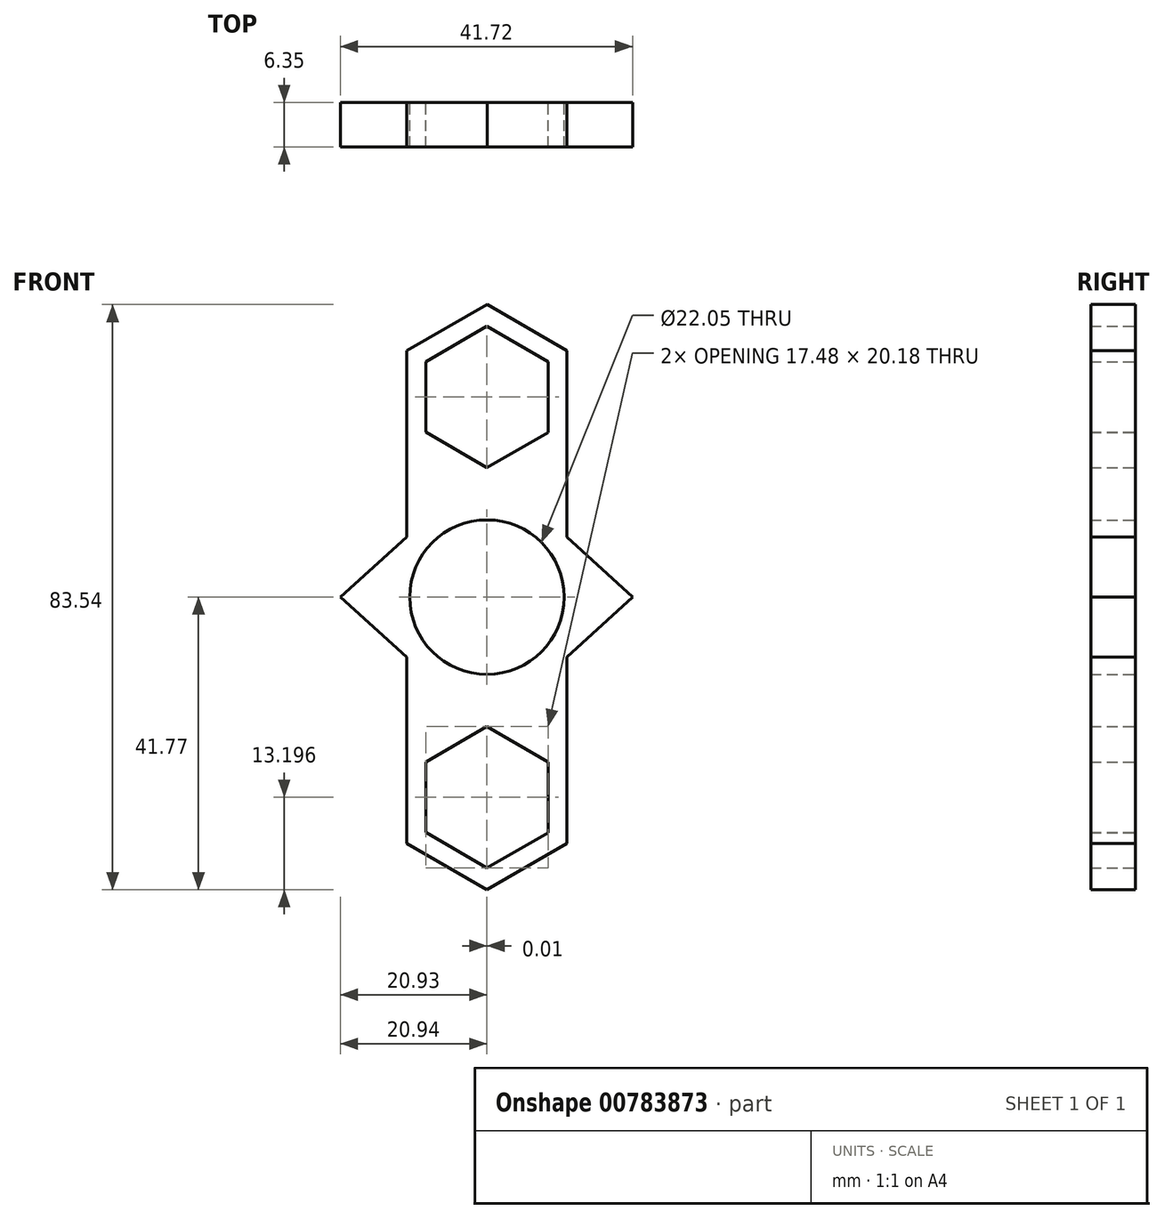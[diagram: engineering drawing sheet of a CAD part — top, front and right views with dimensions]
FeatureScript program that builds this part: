
annotation { "Feature Type Name" : "Feature", "Feature Type Description" : "" }
export const myFeature = defineFeature(function(context is Context, id is Id, definition is map)
    precondition{}
    {
        {
            var Q0;
            Q0=qCreatedBy(makeId("Front.planeOp"),FACE);
            var sketch = newSketch(context, id + "F0", { "sketchPlane" : qUnion([Q0])});
            skCircle(sketch, "E0", {"center": v(0, 0) * mm, "radius": 11.02 * mm});
            skCircle(sketch, "E1", {"center": v(0, 0) * mm, "radius": 14.29 * mm});
            skLineSegment(sketch, "E2", {"start": v(0, 28.58) * mm, "end": v(0, 0) * mm});
            skCircle(sketch, "E3.cCircle", {"center": v(0, 28.58) * mm, "radius": 11.43 * mm, "construction": true});
            skLineSegment(sketch, "E3.0", {"start": v(-0.01, 15.38) * mm, "end": v(-11.44, 21.98) * mm});
            skLineSegment(sketch, "E3.1", {"start": v(-11.44, 21.98) * mm, "end": v(-11.42, 35.18) * mm});
            skLineSegment(sketch, "E3.2", {"start": v(-11.42, 35.18) * mm, "end": v(0.01, 41.77) * mm});
            skLineSegment(sketch, "E3.3", {"start": v(0.01, 41.77) * mm, "end": v(11.44, 35.17) * mm});
            skLineSegment(sketch, "E3.4", {"start": v(11.44, 35.17) * mm, "end": v(11.42, 21.97) * mm});
            skLineSegment(sketch, "E3.5", {"start": v(11.42, 21.97) * mm, "end": v(-0.01, 15.38) * mm});
            skPoint(sketch, "E3.0.midPoint", {"position": v(-5.72, 18.68) * mm});
            skCircle(sketch, "E4.cCircle", {"center": v(0, 28.58) * mm, "radius": 8.74 * mm, "construction": true});
            skLineSegment(sketch, "E4.0", {"start": v(0, 18.49) * mm, "end": v(-8.74, 23.54) * mm});
            skLineSegment(sketch, "E4.1", {"start": v(-8.74, 23.54) * mm, "end": v(-8.73, 33.62) * mm});
            skLineSegment(sketch, "E4.2", {"start": v(-8.73, 33.62) * mm, "end": v(0, 38.66) * mm});
            skLineSegment(sketch, "E4.3", {"start": v(0, 38.66) * mm, "end": v(8.74, 33.61) * mm});
            skLineSegment(sketch, "E4.4", {"start": v(8.74, 33.61) * mm, "end": v(8.73, 23.53) * mm});
            skLineSegment(sketch, "E4.5", {"start": v(8.73, 23.53) * mm, "end": v(0, 18.49) * mm});
            skPoint(sketch, "E4.0.midPoint", {"position": v(-4.37, 21.01) * mm});
            skPoint(sketch, "E5.1.0", {"position": v(5.71, -18.68) * mm});
            skPoint(sketch, "E5.1.1", {"position": v(4.36, -21) * mm});
            skLineSegment(sketch, "E5.1.2", {"start": v(0, -15.38) * mm, "end": v(11.42, -21.98) * mm});
            skLineSegment(sketch, "E5.1.3", {"start": v(11.42, -21.98) * mm, "end": v(11.41, -35.18) * mm});
            skLineSegment(sketch, "E5.1.4", {"start": v(-11.45, -35.16) * mm, "end": v(-11.44, -21.97) * mm});
            skLineSegment(sketch, "E5.1.5", {"start": v(-11.44, -21.97) * mm, "end": v(0, -15.38) * mm});
            skCircle(sketch, "E5.1.6", {"center": v(-0.01, -28.57) * mm, "radius": 8.74 * mm, "construction": true});
            skLineSegment(sketch, "E5.1.7", {"start": v(8.73, -23.53) * mm, "end": v(8.72, -33.62) * mm});
            skLineSegment(sketch, "E5.1.8", {"start": v(-8.75, -23.52) * mm, "end": v(0, -18.48) * mm});
            skLineSegment(sketch, "E5.1.9", {"start": v(-8.75, -33.61) * mm, "end": v(-8.75, -23.52) * mm});
            skLineSegment(sketch, "E5.1.10", {"start": v(0, -18.48) * mm, "end": v(8.73, -23.53) * mm});
            skLineSegment(sketch, "E5.1.11", {"start": v(8.72, -33.62) * mm, "end": v(-0.02, -38.66) * mm});
            skLineSegment(sketch, "E5.1.12", {"start": v(-0.02, -41.77) * mm, "end": v(-11.45, -35.16) * mm});
            skCircle(sketch, "E5.1.13", {"center": v(-0.01, -28.57) * mm, "radius": 11.43 * mm, "construction": true});
            skLineSegment(sketch, "E5.1.14", {"start": v(11.41, -35.18) * mm, "end": v(-0.02, -41.77) * mm});
            skLineSegment(sketch, "E5.1.15", {"start": v(-0.02, -38.66) * mm, "end": v(-8.75, -33.61) * mm});
            skLineSegment(sketch, "E6", {"start": v(-11.44, 21.98) * mm, "end": v(-11.44, 8.57) * mm});
            skLineSegment(sketch, "E7", {"start": v(11.42, 21.97) * mm, "end": v(11.42, 8.58) * mm});
            skLineSegment(sketch, "E8", {"start": v(-11.44, -21.97) * mm, "end": v(-11.44, -8.57) * mm});
            skLineSegment(sketch, "E9", {"start": v(11.42, -21.98) * mm, "end": v(11.42, -8.58) * mm});
            skLineSegment(sketch, "E10", {"start": v(11.42, 8.58) * mm, "end": v(20.78, 0) * mm});
            skLineSegment(sketch, "E11", {"start": v(20.78, 0) * mm, "end": v(11.42, -8.58) * mm});
            skLineSegment(sketch, "E12", {"start": v(-11.44, 8.57) * mm, "end": v(-20.94, 0) * mm});
            skLineSegment(sketch, "E13", {"start": v(-20.94, 0) * mm, "end": v(-11.44, -8.57) * mm});
            skSolve(sketch);
        }
        {
            var Q0;
            Q0 = qSketchRegion(id + "F0", true);
            extrude(context, id + "F1", {"entities" : qUnion([Q0]), "depth" : 6.35 * mm, "offsetDistance" : 25.4 * mm});
        }
    });
